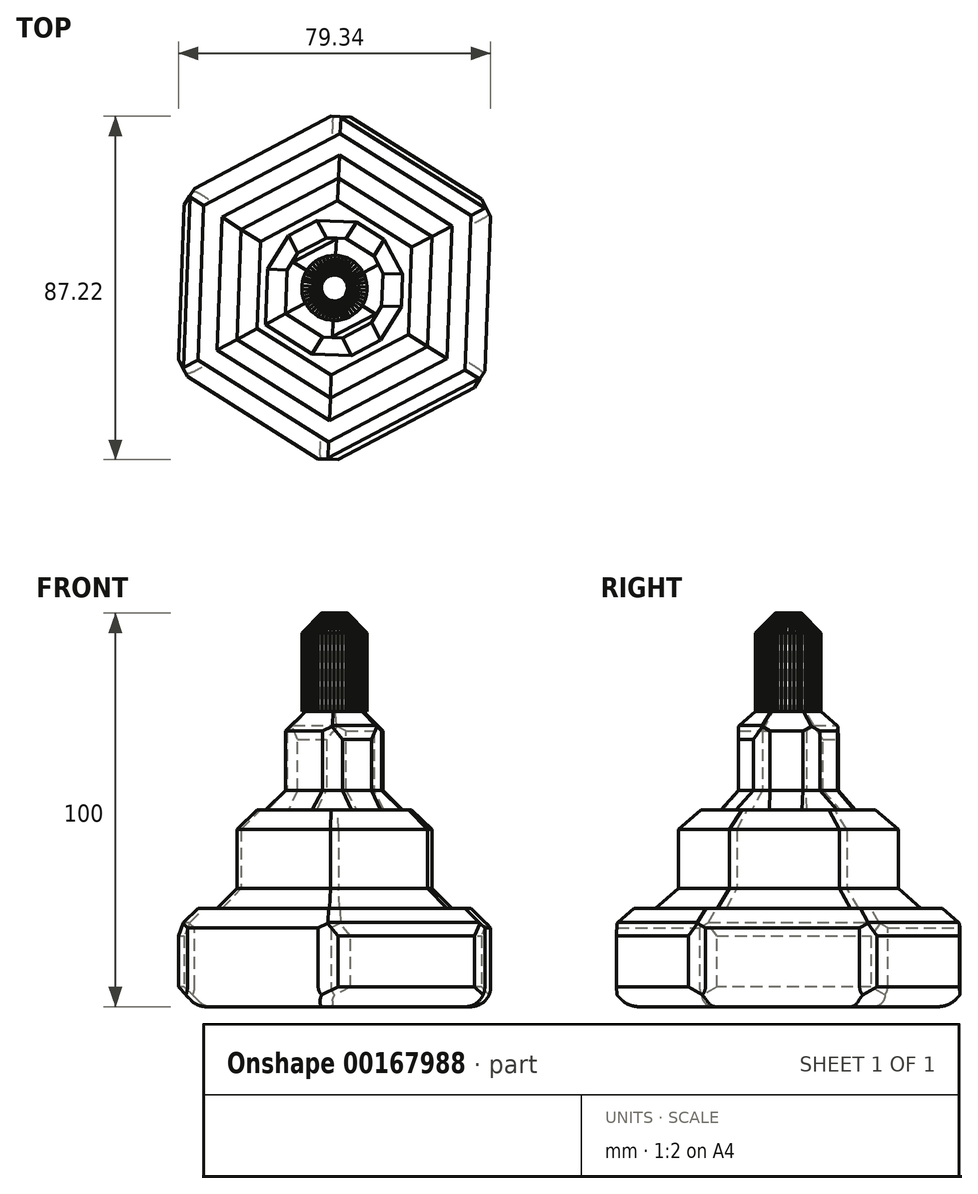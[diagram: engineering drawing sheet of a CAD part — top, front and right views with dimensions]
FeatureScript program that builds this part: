
annotation { "Feature Type Name" : "Feature", "Feature Type Description" : "" }
export const myFeature = defineFeature(function(context is Context, id is Id, definition is map)
    precondition{}
    {
        {
            var Q0;
            Q0=qCreatedBy(makeId("Top.planeOp"),FACE);
            var sketch = newSketch(context, id + "F0", { "sketchPlane" : qUnion([Q0])});
            skCircle(sketch, "E0.cCircle", {"center": v(0, 0) * mm, "radius": 38.96 * mm, "construction": true});
            skLineSegment(sketch, "E0.0", {"start": v(1.69, 44.96) * mm, "end": v(39.78, 21.02) * mm});
            skLineSegment(sketch, "E0.1", {"start": v(39.78, 21.02) * mm, "end": v(38.1, -23.94) * mm});
            skLineSegment(sketch, "E0.2", {"start": v(38.1, -23.94) * mm, "end": v(-1.69, -44.96) * mm});
            skLineSegment(sketch, "E0.3", {"start": v(-1.69, -44.96) * mm, "end": v(-39.78, -21.02) * mm});
            skLineSegment(sketch, "E0.4", {"start": v(-39.78, -21.02) * mm, "end": v(-38.1, 23.94) * mm});
            skLineSegment(sketch, "E0.5", {"start": v(-38.1, 23.94) * mm, "end": v(1.69, 44.96) * mm});
            skPoint(sketch, "E0.0.midPoint", {"position": v(20.74, 32.99) * mm});
            skSolve(sketch);
        }
        {
            var Q0;
            Q0=makeQuery(id+"F0.imprint","IMPRINT",FACE,{"disambiguationData":[TD([[makeQuery(id+"F0.imprint","IMPRINT",EDGE,{"derivedFrom":sQuery(id+"F0.wireOp",EDGE,"E0.0")}),-1.0]])]});
            extrude(context, id + "F1", {"entities" : qUnion([Q0]), "depth" : 25 * mm, "offsetDistance" : 25 * mm});
        }
        {
            var Q0;
            Q0=makeQuery(id+"F1.opExtrude","CAP_FACE",FACE,{"disambiguationData":[OSD([sQuery(id+"F0.wireOp",EDGE,"E0.0"),sQuery(id+"F0.wireOp",EDGE,"E0.1"),sQuery(id+"F0.wireOp",EDGE,"E0.2"),sQuery(id+"F0.wireOp",EDGE,"E0.3"),sQuery(id+"F0.wireOp",EDGE,"E0.4"),sQuery(id+"F0.wireOp",EDGE,"E0.5")])],"isStart":false});
            var sketch = newSketch(context, id + "F2", { "sketchPlane" : qUnion([Q0])});
            skCircle(sketch, "E1.cCircle", {"center": v(0, 0) * mm, "radius": 24.21 * mm, "construction": true});
            skLineSegment(sketch, "E1.0", {"start": v(24.72, 13.06) * mm, "end": v(23.67, -14.88) * mm});
            skLineSegment(sketch, "E1.1", {"start": v(23.67, -14.88) * mm, "end": v(-1.05, -27.94) * mm});
            skLineSegment(sketch, "E1.2", {"start": v(-1.05, -27.94) * mm, "end": v(-24.72, -13.06) * mm});
            skLineSegment(sketch, "E1.3", {"start": v(-24.72, -13.06) * mm, "end": v(-23.67, 14.88) * mm});
            skLineSegment(sketch, "E1.4", {"start": v(-23.67, 14.88) * mm, "end": v(1.05, 27.94) * mm});
            skLineSegment(sketch, "E1.5", {"start": v(1.05, 27.94) * mm, "end": v(24.72, 13.06) * mm});
            skPoint(sketch, "E1.0.midPoint", {"position": v(24.2, -0.9) * mm});
            skSolve(sketch);
        }
        {
            var Q0;
            Q0=makeQuery(id+"F2.imprint","IMPRINT",FACE,{"disambiguationData":[TD([[makeQuery(id+"F2.imprint","IMPRINT",EDGE,{"derivedFrom":sQuery(id+"F2.wireOp",EDGE,"E1.0")}),-1.0]])]});
            extrude(context, id + "F3", {"entities" : qUnion([Q0]), "operationType" : NewBodyOperationType.ADD, "depth" : 25 * mm, "offsetDistance" : 25 * mm});
        }
        {
            var Q0;
            Q0=makeQuery(id+"F3.opExtrude","CAP_FACE",FACE,{"disambiguationData":[OSD([sQuery(id+"F2.wireOp",EDGE,"E1.0"),sQuery(id+"F2.wireOp",EDGE,"E1.1"),sQuery(id+"F2.wireOp",EDGE,"E1.2"),sQuery(id+"F2.wireOp",EDGE,"E1.3"),sQuery(id+"F2.wireOp",EDGE,"E1.4"),sQuery(id+"F2.wireOp",EDGE,"E1.5")])],"isStart":false});
            var sketch = newSketch(context, id + "F4", { "sketchPlane" : qUnion([Q0])});
            skCircle(sketch, "E2.cCircle", {"center": v(0, 0) * mm, "radius": 12.18 * mm, "construction": true});
            skLineSegment(sketch, "E2.0", {"start": v(0.53, 14.05) * mm, "end": v(12.43, 6.57) * mm});
            skLineSegment(sketch, "E2.1", {"start": v(12.43, 6.57) * mm, "end": v(11.9, -7.48) * mm});
            skLineSegment(sketch, "E2.2", {"start": v(11.9, -7.48) * mm, "end": v(-0.53, -14.05) * mm});
            skLineSegment(sketch, "E2.3", {"start": v(-0.53, -14.05) * mm, "end": v(-12.43, -6.57) * mm});
            skLineSegment(sketch, "E2.4", {"start": v(-12.43, -6.57) * mm, "end": v(-11.9, 7.48) * mm});
            skLineSegment(sketch, "E2.5", {"start": v(-11.9, 7.48) * mm, "end": v(0.53, 14.05) * mm});
            skPoint(sketch, "E2.0.midPoint", {"position": v(6.48, 10.31) * mm});
            skSolve(sketch);
        }
        {
            var Q0;
            Q0=makeQuery(id+"F4.imprint","IMPRINT",FACE,{"disambiguationData":[TD([[makeQuery(id+"F4.imprint","IMPRINT",EDGE,{"derivedFrom":sQuery(id+"F4.wireOp",EDGE,"E2.0")}),-1.0]])]});
            extrude(context, id + "F5", {"entities" : qUnion([Q0]), "operationType" : NewBodyOperationType.ADD, "depth" : 25 * mm, "offsetDistance" : 25 * mm});
        }
        {
            var Q0;
            Q0=makeQuery(id+"F3.opExtrude","CAP_EDGE",EDGE,{"disambiguationData":[OSD([sQuery(id+"F2.wireOp",EDGE,"E1.2")])],"isStart":false});
            var Q1;
            Q1=makeQuery(id+"F3.opExtrude","CAP_EDGE",EDGE,{"disambiguationData":[OSD([sQuery(id+"F2.wireOp",EDGE,"E1.1")])],"isStart":false});
            var Q2;
            Q2=makeQuery(id+"F3.opExtrude","CAP_EDGE",EDGE,{"disambiguationData":[OSD([sQuery(id+"F2.wireOp",EDGE,"E1.3")])],"isStart":false});
            var Q3;
            Q3=makeQuery(id+"F3.opExtrude","CAP_EDGE",EDGE,{"disambiguationData":[OSD([sQuery(id+"F2.wireOp",EDGE,"E1.4")])],"isStart":false});
            var Q4;
            Q4=makeQuery(id+"F3.opExtrude","CAP_EDGE",EDGE,{"disambiguationData":[OSD([sQuery(id+"F2.wireOp",EDGE,"E1.5")])],"isStart":false});
            var Q5;
            Q5=makeQuery(id+"F3.opExtrude","CAP_EDGE",EDGE,{"disambiguationData":[OSD([sQuery(id+"F2.wireOp",EDGE,"E1.0")])],"isStart":false});
            chamfer(context, id + "F6", {"entities" : qUnion([Q0, Q1, Q2, Q3, Q4, Q5]), "width" : 5 * mm, "tangentPropagation" : true});
        }
        {
            var Q0;
            Q0=makeQuery(id+"F5.opExtrude","CAP_FACE",FACE,{"disambiguationData":[OSD([sQuery(id+"F4.wireOp",EDGE,"E2.0"),sQuery(id+"F4.wireOp",EDGE,"E2.1"),sQuery(id+"F4.wireOp",EDGE,"E2.2"),sQuery(id+"F4.wireOp",EDGE,"E2.3"),sQuery(id+"F4.wireOp",EDGE,"E2.4"),sQuery(id+"F4.wireOp",EDGE,"E2.5")])],"isStart":false});
            chamfer(context, id + "F7", {"entities" : qUnion([Q0]), "width" : 5 * mm, "tangentPropagation" : true});
        }
        {
            var Q0;
            Q0=makeQuery(id+"F1.opExtrude","CAP_FACE",FACE,{"disambiguationData":[OSD([sQuery(id+"F0.wireOp",EDGE,"E0.0"),sQuery(id+"F0.wireOp",EDGE,"E0.1"),sQuery(id+"F0.wireOp",EDGE,"E0.2"),sQuery(id+"F0.wireOp",EDGE,"E0.3"),sQuery(id+"F0.wireOp",EDGE,"E0.4"),sQuery(id+"F0.wireOp",EDGE,"E0.5")])],"isStart":false});
            chamfer(context, id + "F8", {"entities" : qUnion([Q0]), "width" : 5 * mm, "tangentPropagation" : true});
        }
        {
            var Q0;
            Q0=makeQuery(id+"F5.opExtrude","SWEPT_FACE",FACE,{"disambiguationData":[OSD([sQuery(id+"F4.wireOp",EDGE,"E2.5")])]});
            var Q1;
            Q1=makeQuery(id+"F5.opExtrude","SWEPT_EDGE",EDGE,{"disambiguationData":[OSD([sQuery(id+"F4.wireOp",EDGE,"E2.0"),sQuery(id+"F4.wireOp",EDGE,"E2.1")])]});
            var Q2;
            Q2=makeQuery(id+"F5.opExtrude","SWEPT_FACE",FACE,{"disambiguationData":[OSD([sQuery(id+"F4.wireOp",EDGE,"E2.2")])]});
            var Q3;
            Q3=makeQuery(id+"F1.opExtrude","SWEPT_FACE",FACE,{"disambiguationData":[OSD([sQuery(id+"F0.wireOp",EDGE,"E0.0")])]});
            var Q4;
            Q4=makeQuery(id+"F1.opExtrude","SWEPT_FACE",FACE,{"disambiguationData":[OSD([sQuery(id+"F0.wireOp",EDGE,"E0.2")])]});
            var Q5;
            Q5=makeQuery(id+"F1.opExtrude","SWEPT_FACE",FACE,{"disambiguationData":[OSD([sQuery(id+"F0.wireOp",EDGE,"E0.4")])]});
            chamfer(context, id + "F9", {"entities" : qUnion([Q0, Q1, Q2, Q3, Q4, Q5]), "width" : 5 * mm, "tangentPropagation" : true});
        }
        {
            var Q0;
            Q0=makeQuery(id+"F1.opExtrude","CAP_FACE",FACE,{"disambiguationData":[OSD([sQuery(id+"F0.wireOp",EDGE,"E0.0"),sQuery(id+"F0.wireOp",EDGE,"E0.1"),sQuery(id+"F0.wireOp",EDGE,"E0.2"),sQuery(id+"F0.wireOp",EDGE,"E0.3"),sQuery(id+"F0.wireOp",EDGE,"E0.4"),sQuery(id+"F0.wireOp",EDGE,"E0.5")])],"isStart":true});
            fillet(context, id + "F10", {"entities" : qUnion([Q0]), "tangentPropagation" : true, "radius" : 5 * mm, "defaultsChanged" : false, "vertexSettings" : [], "allowEdgeOverflow" : false});
        }
        {
            var Q0;
            Q0=makeQuery(id+"F5.opExtrude","CAP_FACE",FACE,{"disambiguationData":[OSD([sQuery(id+"F4.wireOp",EDGE,"E2.0"),sQuery(id+"F4.wireOp",EDGE,"E2.1"),sQuery(id+"F4.wireOp",EDGE,"E2.2"),sQuery(id+"F4.wireOp",EDGE,"E2.3"),sQuery(id+"F4.wireOp",EDGE,"E2.4"),sQuery(id+"F4.wireOp",EDGE,"E2.5")])],"isStart":false});
            var sketch = newSketch(context, id + "F11", { "sketchPlane" : qUnion([Q0])});
            skCircle(sketch, "E3.cCircle", {"center": v(0, 0) * mm, "radius": 8.29 * mm, "construction": true});
            skLineSegment(sketch, "E3.0", {"start": v(-7.09, -4.33) * mm, "end": v(-7.57, -3.41) * mm});
            skLineSegment(sketch, "E3.1", {"start": v(-7.57, -3.41) * mm, "end": v(-7.94, -2.43) * mm});
            skLineSegment(sketch, "E3.2", {"start": v(-7.94, -2.43) * mm, "end": v(-8.18, -1.42) * mm});
            skLineSegment(sketch, "E3.3", {"start": v(-8.18, -1.42) * mm, "end": v(-8.3, -0.38) * mm});
            skLineSegment(sketch, "E3.4", {"start": v(-8.3, -0.38) * mm, "end": v(-8.28, 0.66) * mm});
            skLineSegment(sketch, "E3.5", {"start": v(-8.28, 0.66) * mm, "end": v(-8.13, 1.7) * mm});
            skLineSegment(sketch, "E3.6", {"start": v(-8.13, 1.7) * mm, "end": v(-7.86, 2.7) * mm});
            skLineSegment(sketch, "E3.7", {"start": v(-7.86, 2.7) * mm, "end": v(-7.46, 3.66) * mm});
            skLineSegment(sketch, "E3.8", {"start": v(-7.46, 3.66) * mm, "end": v(-6.94, 4.57) * mm});
            skLineSegment(sketch, "E3.9", {"start": v(-6.94, 4.57) * mm, "end": v(-6.31, 5.4) * mm});
            skLineSegment(sketch, "E3.10", {"start": v(-6.31, 5.4) * mm, "end": v(-5.58, 6.15) * mm});
            skLineSegment(sketch, "E3.11", {"start": v(-5.58, 6.15) * mm, "end": v(-4.77, 6.8) * mm});
            skLineSegment(sketch, "E3.12", {"start": v(-4.77, 6.8) * mm, "end": v(-3.88, 7.34) * mm});
            skLineSegment(sketch, "E3.13", {"start": v(-3.88, 7.34) * mm, "end": v(-2.93, 7.77) * mm});
            skLineSegment(sketch, "E3.14", {"start": v(-2.93, 7.77) * mm, "end": v(-1.93, 8.08) * mm});
            skLineSegment(sketch, "E3.15", {"start": v(-1.93, 8.08) * mm, "end": v(-0.9, 8.26) * mm});
            skLineSegment(sketch, "E3.16", {"start": v(-0.9, 8.26) * mm, "end": v(0.14, 8.3) * mm});
            skLineSegment(sketch, "E3.17", {"start": v(0.14, 8.3) * mm, "end": v(1.18, 8.22) * mm});
            skLineSegment(sketch, "E3.18", {"start": v(1.18, 8.22) * mm, "end": v(2.2, 8) * mm});
            skLineSegment(sketch, "E3.19", {"start": v(2.2, 8) * mm, "end": v(3.19, 7.67) * mm});
            skLineSegment(sketch, "E3.20", {"start": v(3.19, 7.67) * mm, "end": v(4.12, 7.21) * mm});
            skLineSegment(sketch, "E3.21", {"start": v(4.12, 7.21) * mm, "end": v(5, 6.64) * mm});
            skLineSegment(sketch, "E3.22", {"start": v(5, 6.64) * mm, "end": v(5.79, 5.96) * mm});
            skLineSegment(sketch, "E3.23", {"start": v(5.79, 5.96) * mm, "end": v(6.49, 5.19) * mm});
            skLineSegment(sketch, "E3.24", {"start": v(6.49, 5.19) * mm, "end": v(7.09, 4.33) * mm});
            skLineSegment(sketch, "E3.25", {"start": v(7.09, 4.33) * mm, "end": v(7.57, 3.41) * mm});
            skLineSegment(sketch, "E3.26", {"start": v(7.57, 3.41) * mm, "end": v(7.94, 2.43) * mm});
            skLineSegment(sketch, "E3.27", {"start": v(7.94, 2.43) * mm, "end": v(8.18, 1.42) * mm});
            skLineSegment(sketch, "E3.28", {"start": v(8.18, 1.42) * mm, "end": v(8.3, 0.38) * mm});
            skLineSegment(sketch, "E3.29", {"start": v(8.3, 0.38) * mm, "end": v(8.28, -0.66) * mm});
            skLineSegment(sketch, "E3.30", {"start": v(8.28, -0.66) * mm, "end": v(8.13, -1.7) * mm});
            skLineSegment(sketch, "E3.31", {"start": v(8.13, -1.7) * mm, "end": v(7.86, -2.7) * mm});
            skLineSegment(sketch, "E3.32", {"start": v(7.86, -2.7) * mm, "end": v(7.46, -3.66) * mm});
            skLineSegment(sketch, "E3.33", {"start": v(7.46, -3.66) * mm, "end": v(6.94, -4.57) * mm});
            skLineSegment(sketch, "E3.34", {"start": v(6.94, -4.57) * mm, "end": v(6.31, -5.4) * mm});
            skLineSegment(sketch, "E3.35", {"start": v(6.31, -5.4) * mm, "end": v(5.58, -6.15) * mm});
            skLineSegment(sketch, "E3.36", {"start": v(5.58, -6.15) * mm, "end": v(4.77, -6.8) * mm});
            skLineSegment(sketch, "E3.37", {"start": v(4.77, -6.8) * mm, "end": v(3.88, -7.34) * mm});
            skLineSegment(sketch, "E3.38", {"start": v(3.88, -7.34) * mm, "end": v(2.93, -7.77) * mm});
            skLineSegment(sketch, "E3.39", {"start": v(2.93, -7.77) * mm, "end": v(1.93, -8.08) * mm});
            skLineSegment(sketch, "E3.40", {"start": v(1.93, -8.08) * mm, "end": v(0.9, -8.26) * mm});
            skLineSegment(sketch, "E3.41", {"start": v(0.9, -8.26) * mm, "end": v(-0.14, -8.3) * mm});
            skLineSegment(sketch, "E3.42", {"start": v(-0.14, -8.3) * mm, "end": v(-1.18, -8.22) * mm});
            skLineSegment(sketch, "E3.43", {"start": v(-1.18, -8.22) * mm, "end": v(-2.2, -8) * mm});
            skLineSegment(sketch, "E3.44", {"start": v(-2.2, -8) * mm, "end": v(-3.19, -7.67) * mm});
            skLineSegment(sketch, "E3.45", {"start": v(-3.19, -7.67) * mm, "end": v(-4.12, -7.21) * mm});
            skLineSegment(sketch, "E3.46", {"start": v(-4.12, -7.21) * mm, "end": v(-5, -6.64) * mm});
            skLineSegment(sketch, "E3.47", {"start": v(-5, -6.64) * mm, "end": v(-5.79, -5.96) * mm});
            skLineSegment(sketch, "E3.48", {"start": v(-5.79, -5.96) * mm, "end": v(-6.49, -5.19) * mm});
            skLineSegment(sketch, "E3.49", {"start": v(-6.49, -5.19) * mm, "end": v(-7.09, -4.33) * mm});
            skPoint(sketch, "E3.0.midPoint", {"position": v(-7.33, -3.87) * mm});
            skSolve(sketch);
        }
        {
            var Q0;
            Q0 = qSketchRegion(id + "F11", true);
            extrude(context, id + "F12", {"entities" : qUnion([Q0]), "operationType" : NewBodyOperationType.ADD, "depth" : 25 * mm, "offsetDistance" : 25 * mm});
        }
        {
            var Q0;
            Q0=makeQuery(id+"F12.opExtrude","CAP_FACE",FACE,{"disambiguationData":[OSD([sQuery(id+"F11.wireOp",EDGE,"E3.0"),sQuery(id+"F11.wireOp",EDGE,"E3.1"),sQuery(id+"F11.wireOp",EDGE,"E3.2"),sQuery(id+"F11.wireOp",EDGE,"E3.3"),sQuery(id+"F11.wireOp",EDGE,"E3.4"),sQuery(id+"F11.wireOp",EDGE,"E3.5"),sQuery(id+"F11.wireOp",EDGE,"E3.6"),sQuery(id+"F11.wireOp",EDGE,"E3.7"),sQuery(id+"F11.wireOp",EDGE,"E3.8"),sQuery(id+"F11.wireOp",EDGE,"E3.9"),sQuery(id+"F11.wireOp",EDGE,"E3.10"),sQuery(id+"F11.wireOp",EDGE,"E3.11"),sQuery(id+"F11.wireOp",EDGE,"E3.12"),sQuery(id+"F11.wireOp",EDGE,"E3.13"),sQuery(id+"F11.wireOp",EDGE,"E3.14"),sQuery(id+"F11.wireOp",EDGE,"E3.15"),sQuery(id+"F11.wireOp",EDGE,"E3.16"),sQuery(id+"F11.wireOp",EDGE,"E3.17"),sQuery(id+"F11.wireOp",EDGE,"E3.18"),sQuery(id+"F11.wireOp",EDGE,"E3.19"),sQuery(id+"F11.wireOp",EDGE,"E3.20"),sQuery(id+"F11.wireOp",EDGE,"E3.21"),sQuery(id+"F11.wireOp",EDGE,"E3.22"),sQuery(id+"F11.wireOp",EDGE,"E3.23"),sQuery(id+"F11.wireOp",EDGE,"E3.24"),sQuery(id+"F11.wireOp",EDGE,"E3.25"),sQuery(id+"F11.wireOp",EDGE,"E3.26"),sQuery(id+"F11.wireOp",EDGE,"E3.27"),sQuery(id+"F11.wireOp",EDGE,"E3.28"),sQuery(id+"F11.wireOp",EDGE,"E3.29"),sQuery(id+"F11.wireOp",EDGE,"E3.30"),sQuery(id+"F11.wireOp",EDGE,"E3.31"),sQuery(id+"F11.wireOp",EDGE,"E3.32"),sQuery(id+"F11.wireOp",EDGE,"E3.33"),sQuery(id+"F11.wireOp",EDGE,"E3.34"),sQuery(id+"F11.wireOp",EDGE,"E3.35"),sQuery(id+"F11.wireOp",EDGE,"E3.36"),sQuery(id+"F11.wireOp",EDGE,"E3.37"),sQuery(id+"F11.wireOp",EDGE,"E3.38"),sQuery(id+"F11.wireOp",EDGE,"E3.39"),sQuery(id+"F11.wireOp",EDGE,"E3.40"),sQuery(id+"F11.wireOp",EDGE,"E3.41"),sQuery(id+"F11.wireOp",EDGE,"E3.42"),sQuery(id+"F11.wireOp",EDGE,"E3.43"),sQuery(id+"F11.wireOp",EDGE,"E3.44"),sQuery(id+"F11.wireOp",EDGE,"E3.45"),sQuery(id+"F11.wireOp",EDGE,"E3.46"),sQuery(id+"F11.wireOp",EDGE,"E3.47"),sQuery(id+"F11.wireOp",EDGE,"E3.48"),sQuery(id+"F11.wireOp",EDGE,"E3.49")])],"isStart":false});
            chamfer(context, id + "F13", {"entities" : qUnion([Q0]), "width" : 5 * mm, "tangentPropagation" : true});
        }
    });
